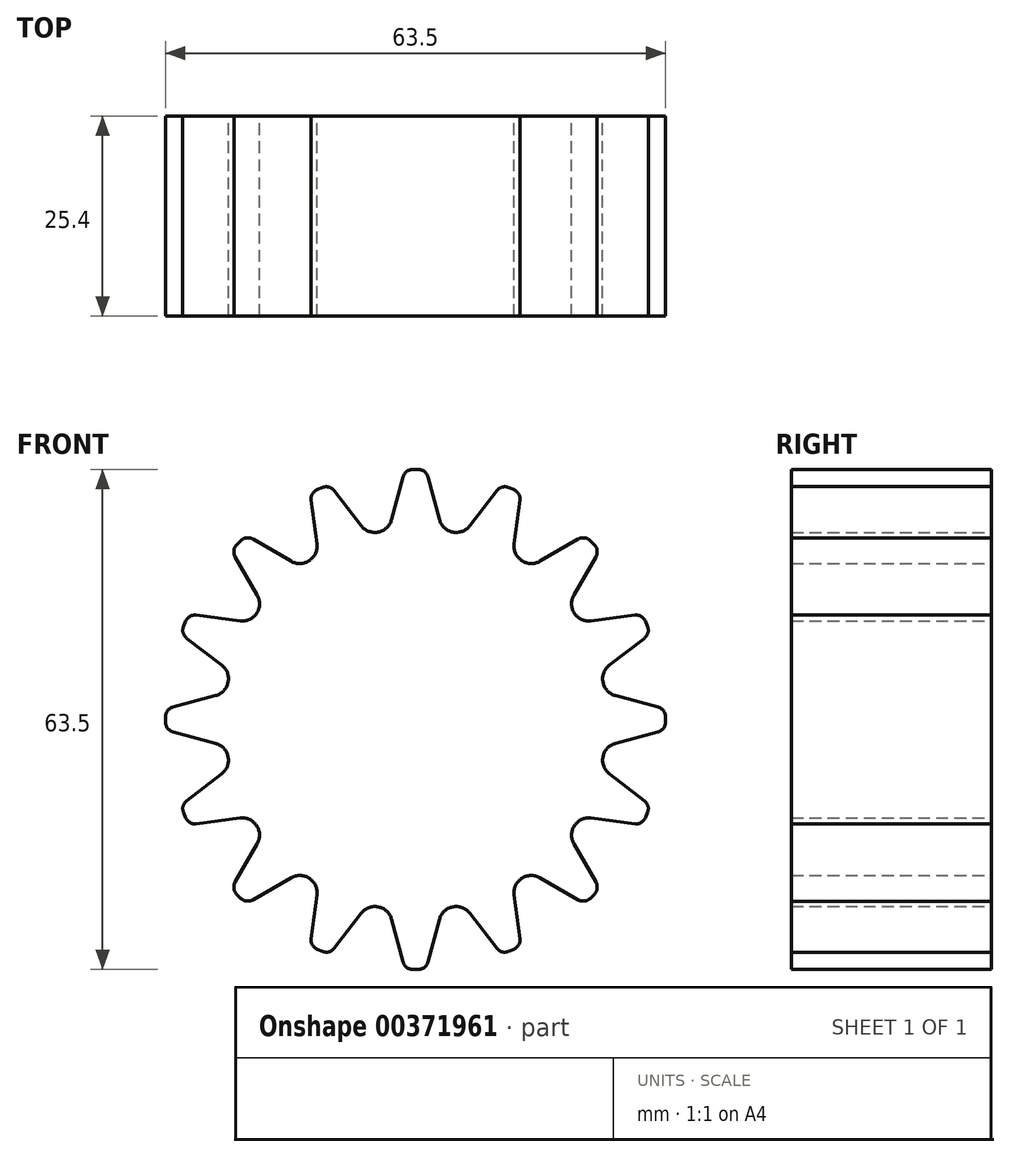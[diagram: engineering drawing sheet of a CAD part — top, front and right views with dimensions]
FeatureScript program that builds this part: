
annotation { "Feature Type Name" : "Feature", "Feature Type Description" : "" }
export const myFeature = defineFeature(function(context is Context, id is Id, definition is map)
    precondition{}
    {
        {
            var Q0;
            Q0=qCreatedBy(makeId("Front.planeOp"),FACE);
            var sketch = newSketch(context, id + "F0", { "sketchPlane" : qUnion([Q0])});
            skLineSegment(sketch, "E0", {"start": v(0, 39.03) * mm, "end": v(0, -39.4) * mm, "construction": true});
            skCircle(sketch, "E1", {"center": v(0, 0) * mm, "radius": 25.4 * mm, "construction": true});
            skLineSegment(sketch, "E2", {"start": v(0, 31.75) * mm, "end": v(-0.36, 31.75) * mm});
            skLineSegment(sketch, "E3", {"start": v(-1.59, 30.8) * mm, "end": v(-3.04, 25.4) * mm});
            skLineSegment(sketch, "E4.MirrorCS", {"start": v(0, 31.75) * mm, "end": v(0.36, 31.75) * mm});
            skLineSegment(sketch, "E5.MirrorCS", {"start": v(1.59, 30.8) * mm, "end": v(3.04, 25.4) * mm});
            skPoint(sketch, "E6.visualSharp", {"position": v(-1.34, 31.75) * mm});
            skArc(sketch, "E6.filletArc", {"start": v(-0.36, 31.75) * mm, "mid": v(-1.13, 31.49) * mm, "end": v(-1.59, 30.8) * mm});
            skPoint(sketch, "E7.visualSharp", {"position": v(1.34, 31.75) * mm});
            skArc(sketch, "E7.filletArc", {"start": v(1.59, 30.8) * mm, "mid": v(1.13, 31.49) * mm, "end": v(0.36, 31.75) * mm});
            skArc(sketch, "E8", {"start": v(3.04, 25.4) * mm, "mid": v(4.74, 23.8) * mm, "end": v(6.91, 24.63) * mm});
            skArc(sketch, "E9.MirrorCS", {"start": v(0.36, 31.75) * mm, "mid": v(1.13, 31.49) * mm, "end": v(1.59, 30.8) * mm});
            skArc(sketch, "E10.MirrorCS", {"start": v(-1.59, 30.8) * mm, "mid": v(-1.13, 31.49) * mm, "end": v(-0.36, 31.75) * mm});
            skLineSegment(sketch, "E11.1.0", {"start": v(-13.26, 27.86) * mm, "end": v(-12.53, 22.3) * mm});
            skArc(sketch, "E11.1.1", {"start": v(-6.91, 24.63) * mm, "mid": v(-4.74, 23.8) * mm, "end": v(-3.04, 25.4) * mm});
            skPoint(sketch, "E11.1.2", {"position": v(-10.92, 29.84) * mm});
            skLineSegment(sketch, "E11.1.3", {"start": v(-10.32, 29.07) * mm, "end": v(-6.91, 24.63) * mm});
            skPoint(sketch, "E11.1.4", {"position": v(-13.38, 28.82) * mm});
            skPoint(sketch, "E11.1.5", {"position": v(-13.38, 28.82) * mm});
            skPoint(sketch, "E11.1.6", {"position": v(-10.92, 29.84) * mm});
            skLineSegment(sketch, "E11.1.7", {"start": v(-13.26, 27.86) * mm, "end": v(-12.53, 22.3) * mm});
            skLineSegment(sketch, "E11.1.8", {"start": v(-10.32, 29.07) * mm, "end": v(-6.91, 24.63) * mm});
            skArc(sketch, "E11.1.9", {"start": v(-13.26, 27.86) * mm, "mid": v(-13.1, 28.66) * mm, "end": v(-12.48, 29.2) * mm});
            skArc(sketch, "E11.1.10", {"start": v(-11.82, 29.47) * mm, "mid": v(-11, 29.52) * mm, "end": v(-10.32, 29.07) * mm});
            skArc(sketch, "E11.1.11", {"start": v(-10.32, 29.07) * mm, "mid": v(-11, 29.52) * mm, "end": v(-11.82, 29.47) * mm});
            skArc(sketch, "E11.1.12", {"start": v(-12.48, 29.2) * mm, "mid": v(-13.1, 28.66) * mm, "end": v(-13.26, 27.86) * mm});
            skLineSegment(sketch, "E11.1.13", {"start": v(-12.15, 29.33) * mm, "end": v(-11.82, 29.47) * mm});
            skLineSegment(sketch, "E11.1.14", {"start": v(-12.15, 29.33) * mm, "end": v(-12.48, 29.2) * mm});
            skLineSegment(sketch, "E11.1.15", {"start": v(-12.15, 29.33) * mm, "end": v(-12.48, 29.2) * mm});
            skLineSegment(sketch, "E11.1.16", {"start": v(-12.15, 29.33) * mm, "end": v(-11.82, 29.47) * mm});
            skLineSegment(sketch, "E11.2.0", {"start": v(-22.9, 20.66) * mm, "end": v(-20.1, 15.81) * mm});
            skArc(sketch, "E11.2.1", {"start": v(-15.81, 20.1) * mm, "mid": v(-13.49, 20.18) * mm, "end": v(-12.53, 22.3) * mm});
            skPoint(sketch, "E11.2.2", {"position": v(-21.5, 23.4) * mm});
            skLineSegment(sketch, "E11.2.3", {"start": v(-20.66, 22.9) * mm, "end": v(-15.81, 20.1) * mm});
            skPoint(sketch, "E11.2.4", {"position": v(-23.4, 21.5) * mm});
            skPoint(sketch, "E11.2.5", {"position": v(-23.4, 21.5) * mm});
            skPoint(sketch, "E11.2.6", {"position": v(-21.5, 23.4) * mm});
            skLineSegment(sketch, "E11.2.7", {"start": v(-22.9, 20.66) * mm, "end": v(-20.1, 15.81) * mm});
            skLineSegment(sketch, "E11.2.8", {"start": v(-20.66, 22.9) * mm, "end": v(-15.81, 20.1) * mm});
            skArc(sketch, "E11.2.9", {"start": v(-22.9, 20.66) * mm, "mid": v(-23.07, 21.46) * mm, "end": v(-22.7, 22.2) * mm});
            skArc(sketch, "E11.2.10", {"start": v(-22.2, 22.7) * mm, "mid": v(-21.46, 23.07) * mm, "end": v(-20.66, 22.9) * mm});
            skArc(sketch, "E11.2.11", {"start": v(-20.66, 22.9) * mm, "mid": v(-21.46, 23.07) * mm, "end": v(-22.2, 22.7) * mm});
            skArc(sketch, "E11.2.12", {"start": v(-22.7, 22.2) * mm, "mid": v(-23.07, 21.46) * mm, "end": v(-22.9, 20.66) * mm});
            skLineSegment(sketch, "E11.2.13", {"start": v(-22.45, 22.45) * mm, "end": v(-22.2, 22.7) * mm});
            skLineSegment(sketch, "E11.2.14", {"start": v(-22.45, 22.45) * mm, "end": v(-22.7, 22.2) * mm});
            skLineSegment(sketch, "E11.2.15", {"start": v(-22.45, 22.45) * mm, "end": v(-22.7, 22.2) * mm});
            skLineSegment(sketch, "E11.2.16", {"start": v(-22.45, 22.45) * mm, "end": v(-22.2, 22.7) * mm});
            skLineSegment(sketch, "E11.3.0", {"start": v(-29.07, 10.32) * mm, "end": v(-24.63, 6.91) * mm});
            skArc(sketch, "E11.3.1", {"start": v(-22.3, 12.53) * mm, "mid": v(-20.18, 13.49) * mm, "end": v(-20.1, 15.81) * mm});
            skPoint(sketch, "E11.3.2", {"position": v(-28.82, 13.38) * mm});
            skLineSegment(sketch, "E11.3.3", {"start": v(-27.86, 13.26) * mm, "end": v(-22.3, 12.53) * mm});
            skPoint(sketch, "E11.3.4", {"position": v(-29.84, 10.92) * mm});
            skPoint(sketch, "E11.3.5", {"position": v(-29.84, 10.92) * mm});
            skPoint(sketch, "E11.3.6", {"position": v(-28.82, 13.38) * mm});
            skLineSegment(sketch, "E11.3.7", {"start": v(-29.07, 10.32) * mm, "end": v(-24.63, 6.91) * mm});
            skLineSegment(sketch, "E11.3.8", {"start": v(-27.86, 13.26) * mm, "end": v(-22.3, 12.53) * mm});
            skArc(sketch, "E11.3.9", {"start": v(-29.07, 10.32) * mm, "mid": v(-29.52, 11) * mm, "end": v(-29.47, 11.82) * mm});
            skArc(sketch, "E11.3.10", {"start": v(-29.2, 12.48) * mm, "mid": v(-28.66, 13.1) * mm, "end": v(-27.86, 13.26) * mm});
            skArc(sketch, "E11.3.11", {"start": v(-27.86, 13.26) * mm, "mid": v(-28.66, 13.1) * mm, "end": v(-29.2, 12.48) * mm});
            skArc(sketch, "E11.3.12", {"start": v(-29.47, 11.82) * mm, "mid": v(-29.52, 11) * mm, "end": v(-29.07, 10.32) * mm});
            skLineSegment(sketch, "E11.3.13", {"start": v(-29.33, 12.15) * mm, "end": v(-29.2, 12.48) * mm});
            skLineSegment(sketch, "E11.3.14", {"start": v(-29.33, 12.15) * mm, "end": v(-29.47, 11.82) * mm});
            skLineSegment(sketch, "E11.3.15", {"start": v(-29.33, 12.15) * mm, "end": v(-29.47, 11.82) * mm});
            skLineSegment(sketch, "E11.3.16", {"start": v(-29.33, 12.15) * mm, "end": v(-29.2, 12.48) * mm});
            skLineSegment(sketch, "E11.4.0", {"start": v(-30.8, -1.59) * mm, "end": v(-25.4, -3.04) * mm});
            skArc(sketch, "E11.4.1", {"start": v(-25.4, 3.04) * mm, "mid": v(-23.8, 4.74) * mm, "end": v(-24.63, 6.91) * mm});
            skPoint(sketch, "E11.4.2", {"position": v(-31.75, 1.34) * mm});
            skLineSegment(sketch, "E11.4.3", {"start": v(-30.8, 1.59) * mm, "end": v(-25.4, 3.04) * mm});
            skPoint(sketch, "E11.4.4", {"position": v(-31.75, -1.34) * mm});
            skPoint(sketch, "E11.4.5", {"position": v(-31.75, -1.34) * mm});
            skPoint(sketch, "E11.4.6", {"position": v(-31.75, 1.34) * mm});
            skLineSegment(sketch, "E11.4.7", {"start": v(-30.8, -1.59) * mm, "end": v(-25.4, -3.04) * mm});
            skLineSegment(sketch, "E11.4.8", {"start": v(-30.8, 1.59) * mm, "end": v(-25.4, 3.04) * mm});
            skArc(sketch, "E11.4.9", {"start": v(-30.8, -1.59) * mm, "mid": v(-31.49, -1.13) * mm, "end": v(-31.75, -0.36) * mm});
            skArc(sketch, "E11.4.10", {"start": v(-31.75, 0.36) * mm, "mid": v(-31.49, 1.13) * mm, "end": v(-30.8, 1.59) * mm});
            skArc(sketch, "E11.4.11", {"start": v(-30.8, 1.59) * mm, "mid": v(-31.49, 1.13) * mm, "end": v(-31.75, 0.36) * mm});
            skArc(sketch, "E11.4.12", {"start": v(-31.75, -0.36) * mm, "mid": v(-31.49, -1.13) * mm, "end": v(-30.8, -1.59) * mm});
            skLineSegment(sketch, "E11.4.13", {"start": v(-31.75, 0) * mm, "end": v(-31.75, 0.36) * mm});
            skLineSegment(sketch, "E11.4.14", {"start": v(-31.75, 0) * mm, "end": v(-31.75, -0.36) * mm});
            skLineSegment(sketch, "E11.4.15", {"start": v(-31.75, 0) * mm, "end": v(-31.75, -0.36) * mm});
            skLineSegment(sketch, "E11.4.16", {"start": v(-31.75, 0) * mm, "end": v(-31.75, 0.36) * mm});
            skLineSegment(sketch, "E11.5.0", {"start": v(-27.86, -13.26) * mm, "end": v(-22.3, -12.53) * mm});
            skArc(sketch, "E11.5.1", {"start": v(-24.63, -6.91) * mm, "mid": v(-23.8, -4.74) * mm, "end": v(-25.4, -3.04) * mm});
            skPoint(sketch, "E11.5.2", {"position": v(-29.84, -10.92) * mm});
            skLineSegment(sketch, "E11.5.3", {"start": v(-29.07, -10.32) * mm, "end": v(-24.63, -6.91) * mm});
            skPoint(sketch, "E11.5.4", {"position": v(-28.82, -13.38) * mm});
            skPoint(sketch, "E11.5.5", {"position": v(-28.82, -13.38) * mm});
            skPoint(sketch, "E11.5.6", {"position": v(-29.84, -10.92) * mm});
            skLineSegment(sketch, "E11.5.7", {"start": v(-27.86, -13.26) * mm, "end": v(-22.3, -12.53) * mm});
            skLineSegment(sketch, "E11.5.8", {"start": v(-29.07, -10.32) * mm, "end": v(-24.63, -6.91) * mm});
            skArc(sketch, "E11.5.9", {"start": v(-27.86, -13.26) * mm, "mid": v(-28.66, -13.1) * mm, "end": v(-29.2, -12.48) * mm});
            skArc(sketch, "E11.5.10", {"start": v(-29.47, -11.82) * mm, "mid": v(-29.52, -11) * mm, "end": v(-29.07, -10.32) * mm});
            skArc(sketch, "E11.5.11", {"start": v(-29.07, -10.32) * mm, "mid": v(-29.52, -11) * mm, "end": v(-29.47, -11.82) * mm});
            skArc(sketch, "E11.5.12", {"start": v(-29.2, -12.48) * mm, "mid": v(-28.66, -13.1) * mm, "end": v(-27.86, -13.26) * mm});
            skLineSegment(sketch, "E11.5.13", {"start": v(-29.33, -12.15) * mm, "end": v(-29.47, -11.82) * mm});
            skLineSegment(sketch, "E11.5.14", {"start": v(-29.33, -12.15) * mm, "end": v(-29.2, -12.48) * mm});
            skLineSegment(sketch, "E11.5.15", {"start": v(-29.33, -12.15) * mm, "end": v(-29.2, -12.48) * mm});
            skLineSegment(sketch, "E11.5.16", {"start": v(-29.33, -12.15) * mm, "end": v(-29.47, -11.82) * mm});
            skLineSegment(sketch, "E11.6.0", {"start": v(-20.66, -22.9) * mm, "end": v(-15.81, -20.1) * mm});
            skArc(sketch, "E11.6.1", {"start": v(-20.1, -15.81) * mm, "mid": v(-20.18, -13.49) * mm, "end": v(-22.3, -12.53) * mm});
            skPoint(sketch, "E11.6.2", {"position": v(-23.4, -21.5) * mm});
            skLineSegment(sketch, "E11.6.3", {"start": v(-22.9, -20.66) * mm, "end": v(-20.1, -15.81) * mm});
            skPoint(sketch, "E11.6.4", {"position": v(-21.5, -23.4) * mm});
            skPoint(sketch, "E11.6.5", {"position": v(-21.5, -23.4) * mm});
            skPoint(sketch, "E11.6.6", {"position": v(-23.4, -21.5) * mm});
            skLineSegment(sketch, "E11.6.7", {"start": v(-20.66, -22.9) * mm, "end": v(-15.81, -20.1) * mm});
            skLineSegment(sketch, "E11.6.8", {"start": v(-22.9, -20.66) * mm, "end": v(-20.1, -15.81) * mm});
            skArc(sketch, "E11.6.9", {"start": v(-20.66, -22.9) * mm, "mid": v(-21.46, -23.07) * mm, "end": v(-22.2, -22.7) * mm});
            skArc(sketch, "E11.6.10", {"start": v(-22.7, -22.2) * mm, "mid": v(-23.07, -21.46) * mm, "end": v(-22.9, -20.66) * mm});
            skArc(sketch, "E11.6.11", {"start": v(-22.9, -20.66) * mm, "mid": v(-23.07, -21.46) * mm, "end": v(-22.7, -22.2) * mm});
            skArc(sketch, "E11.6.12", {"start": v(-22.2, -22.7) * mm, "mid": v(-21.46, -23.07) * mm, "end": v(-20.66, -22.9) * mm});
            skLineSegment(sketch, "E11.6.13", {"start": v(-22.45, -22.45) * mm, "end": v(-22.7, -22.2) * mm});
            skLineSegment(sketch, "E11.6.14", {"start": v(-22.45, -22.45) * mm, "end": v(-22.2, -22.7) * mm});
            skLineSegment(sketch, "E11.6.15", {"start": v(-22.45, -22.45) * mm, "end": v(-22.2, -22.7) * mm});
            skLineSegment(sketch, "E11.6.16", {"start": v(-22.45, -22.45) * mm, "end": v(-22.7, -22.2) * mm});
            skLineSegment(sketch, "E11.7.0", {"start": v(-10.32, -29.07) * mm, "end": v(-6.91, -24.63) * mm});
            skArc(sketch, "E11.7.1", {"start": v(-12.53, -22.3) * mm, "mid": v(-13.49, -20.18) * mm, "end": v(-15.81, -20.1) * mm});
            skPoint(sketch, "E11.7.2", {"position": v(-13.38, -28.82) * mm});
            skLineSegment(sketch, "E11.7.3", {"start": v(-13.26, -27.86) * mm, "end": v(-12.53, -22.3) * mm});
            skPoint(sketch, "E11.7.4", {"position": v(-10.92, -29.84) * mm});
            skPoint(sketch, "E11.7.5", {"position": v(-10.92, -29.84) * mm});
            skPoint(sketch, "E11.7.6", {"position": v(-13.38, -28.82) * mm});
            skLineSegment(sketch, "E11.7.7", {"start": v(-10.32, -29.07) * mm, "end": v(-6.91, -24.63) * mm});
            skLineSegment(sketch, "E11.7.8", {"start": v(-13.26, -27.86) * mm, "end": v(-12.53, -22.3) * mm});
            skArc(sketch, "E11.7.9", {"start": v(-10.32, -29.07) * mm, "mid": v(-11, -29.52) * mm, "end": v(-11.82, -29.47) * mm});
            skArc(sketch, "E11.7.10", {"start": v(-12.48, -29.2) * mm, "mid": v(-13.1, -28.66) * mm, "end": v(-13.26, -27.86) * mm});
            skArc(sketch, "E11.7.11", {"start": v(-13.26, -27.86) * mm, "mid": v(-13.1, -28.66) * mm, "end": v(-12.48, -29.2) * mm});
            skArc(sketch, "E11.7.12", {"start": v(-11.82, -29.47) * mm, "mid": v(-11, -29.52) * mm, "end": v(-10.32, -29.07) * mm});
            skLineSegment(sketch, "E11.7.13", {"start": v(-12.15, -29.33) * mm, "end": v(-12.48, -29.2) * mm});
            skLineSegment(sketch, "E11.7.14", {"start": v(-12.15, -29.33) * mm, "end": v(-11.82, -29.47) * mm});
            skLineSegment(sketch, "E11.7.15", {"start": v(-12.15, -29.33) * mm, "end": v(-11.82, -29.47) * mm});
            skLineSegment(sketch, "E11.7.16", {"start": v(-12.15, -29.33) * mm, "end": v(-12.48, -29.2) * mm});
            skLineSegment(sketch, "E11.8.0", {"start": v(1.59, -30.8) * mm, "end": v(3.04, -25.4) * mm});
            skArc(sketch, "E11.8.1", {"start": v(-3.04, -25.4) * mm, "mid": v(-4.74, -23.8) * mm, "end": v(-6.91, -24.63) * mm});
            skPoint(sketch, "E11.8.2", {"position": v(-1.34, -31.75) * mm});
            skLineSegment(sketch, "E11.8.3", {"start": v(-1.59, -30.8) * mm, "end": v(-3.04, -25.4) * mm});
            skPoint(sketch, "E11.8.4", {"position": v(1.34, -31.75) * mm});
            skPoint(sketch, "E11.8.5", {"position": v(1.34, -31.75) * mm});
            skPoint(sketch, "E11.8.6", {"position": v(-1.34, -31.75) * mm});
            skLineSegment(sketch, "E11.8.7", {"start": v(1.59, -30.8) * mm, "end": v(3.04, -25.4) * mm});
            skLineSegment(sketch, "E11.8.8", {"start": v(-1.59, -30.8) * mm, "end": v(-3.04, -25.4) * mm});
            skArc(sketch, "E11.8.9", {"start": v(1.59, -30.8) * mm, "mid": v(1.13, -31.49) * mm, "end": v(0.36, -31.75) * mm});
            skArc(sketch, "E11.8.10", {"start": v(-0.36, -31.75) * mm, "mid": v(-1.13, -31.49) * mm, "end": v(-1.59, -30.8) * mm});
            skArc(sketch, "E11.8.11", {"start": v(-1.59, -30.8) * mm, "mid": v(-1.13, -31.49) * mm, "end": v(-0.36, -31.75) * mm});
            skArc(sketch, "E11.8.12", {"start": v(0.36, -31.75) * mm, "mid": v(1.13, -31.49) * mm, "end": v(1.59, -30.8) * mm});
            skLineSegment(sketch, "E11.8.13", {"start": v(0, -31.75) * mm, "end": v(-0.36, -31.75) * mm});
            skLineSegment(sketch, "E11.8.14", {"start": v(0, -31.75) * mm, "end": v(0.36, -31.75) * mm});
            skLineSegment(sketch, "E11.8.15", {"start": v(0, -31.75) * mm, "end": v(0.36, -31.75) * mm});
            skLineSegment(sketch, "E11.8.16", {"start": v(0, -31.75) * mm, "end": v(-0.36, -31.75) * mm});
            skLineSegment(sketch, "E11.9.0", {"start": v(13.26, -27.86) * mm, "end": v(12.53, -22.3) * mm});
            skArc(sketch, "E11.9.1", {"start": v(6.91, -24.63) * mm, "mid": v(4.74, -23.8) * mm, "end": v(3.04, -25.4) * mm});
            skPoint(sketch, "E11.9.2", {"position": v(10.92, -29.84) * mm});
            skLineSegment(sketch, "E11.9.3", {"start": v(10.32, -29.07) * mm, "end": v(6.91, -24.63) * mm});
            skPoint(sketch, "E11.9.4", {"position": v(13.38, -28.82) * mm});
            skPoint(sketch, "E11.9.5", {"position": v(13.38, -28.82) * mm});
            skPoint(sketch, "E11.9.6", {"position": v(10.92, -29.84) * mm});
            skLineSegment(sketch, "E11.9.7", {"start": v(13.26, -27.86) * mm, "end": v(12.53, -22.3) * mm});
            skLineSegment(sketch, "E11.9.8", {"start": v(10.32, -29.07) * mm, "end": v(6.91, -24.63) * mm});
            skArc(sketch, "E11.9.9", {"start": v(13.26, -27.86) * mm, "mid": v(13.1, -28.66) * mm, "end": v(12.48, -29.2) * mm});
            skArc(sketch, "E11.9.10", {"start": v(11.82, -29.47) * mm, "mid": v(11, -29.52) * mm, "end": v(10.32, -29.07) * mm});
            skArc(sketch, "E11.9.11", {"start": v(10.32, -29.07) * mm, "mid": v(11, -29.52) * mm, "end": v(11.82, -29.47) * mm});
            skArc(sketch, "E11.9.12", {"start": v(12.48, -29.2) * mm, "mid": v(13.1, -28.66) * mm, "end": v(13.26, -27.86) * mm});
            skLineSegment(sketch, "E11.9.13", {"start": v(12.15, -29.33) * mm, "end": v(11.82, -29.47) * mm});
            skLineSegment(sketch, "E11.9.14", {"start": v(12.15, -29.33) * mm, "end": v(12.48, -29.2) * mm});
            skLineSegment(sketch, "E11.9.15", {"start": v(12.15, -29.33) * mm, "end": v(12.48, -29.2) * mm});
            skLineSegment(sketch, "E11.9.16", {"start": v(12.15, -29.33) * mm, "end": v(11.82, -29.47) * mm});
            skLineSegment(sketch, "E11.10.0", {"start": v(22.9, -20.66) * mm, "end": v(20.1, -15.81) * mm});
            skArc(sketch, "E11.10.1", {"start": v(15.81, -20.1) * mm, "mid": v(13.49, -20.18) * mm, "end": v(12.53, -22.3) * mm});
            skPoint(sketch, "E11.10.2", {"position": v(21.5, -23.4) * mm});
            skLineSegment(sketch, "E11.10.3", {"start": v(20.66, -22.9) * mm, "end": v(15.81, -20.1) * mm});
            skPoint(sketch, "E11.10.4", {"position": v(23.4, -21.5) * mm});
            skPoint(sketch, "E11.10.5", {"position": v(23.4, -21.5) * mm});
            skPoint(sketch, "E11.10.6", {"position": v(21.5, -23.4) * mm});
            skLineSegment(sketch, "E11.10.7", {"start": v(22.9, -20.66) * mm, "end": v(20.1, -15.81) * mm});
            skLineSegment(sketch, "E11.10.8", {"start": v(20.66, -22.9) * mm, "end": v(15.81, -20.1) * mm});
            skArc(sketch, "E11.10.9", {"start": v(22.9, -20.66) * mm, "mid": v(23.07, -21.46) * mm, "end": v(22.7, -22.2) * mm});
            skArc(sketch, "E11.10.10", {"start": v(22.2, -22.7) * mm, "mid": v(21.46, -23.07) * mm, "end": v(20.66, -22.9) * mm});
            skArc(sketch, "E11.10.11", {"start": v(20.66, -22.9) * mm, "mid": v(21.46, -23.07) * mm, "end": v(22.2, -22.7) * mm});
            skArc(sketch, "E11.10.12", {"start": v(22.7, -22.2) * mm, "mid": v(23.07, -21.46) * mm, "end": v(22.9, -20.66) * mm});
            skLineSegment(sketch, "E11.10.13", {"start": v(22.45, -22.45) * mm, "end": v(22.2, -22.7) * mm});
            skLineSegment(sketch, "E11.10.14", {"start": v(22.45, -22.45) * mm, "end": v(22.7, -22.2) * mm});
            skLineSegment(sketch, "E11.10.15", {"start": v(22.45, -22.45) * mm, "end": v(22.7, -22.2) * mm});
            skLineSegment(sketch, "E11.10.16", {"start": v(22.45, -22.45) * mm, "end": v(22.2, -22.7) * mm});
            skLineSegment(sketch, "E11.11.0", {"start": v(29.07, -10.32) * mm, "end": v(24.63, -6.91) * mm});
            skArc(sketch, "E11.11.1", {"start": v(22.3, -12.53) * mm, "mid": v(20.18, -13.49) * mm, "end": v(20.1, -15.81) * mm});
            skPoint(sketch, "E11.11.2", {"position": v(28.82, -13.38) * mm});
            skLineSegment(sketch, "E11.11.3", {"start": v(27.86, -13.26) * mm, "end": v(22.3, -12.53) * mm});
            skPoint(sketch, "E11.11.4", {"position": v(29.84, -10.92) * mm});
            skPoint(sketch, "E11.11.5", {"position": v(29.84, -10.92) * mm});
            skPoint(sketch, "E11.11.6", {"position": v(28.82, -13.38) * mm});
            skLineSegment(sketch, "E11.11.7", {"start": v(29.07, -10.32) * mm, "end": v(24.63, -6.91) * mm});
            skLineSegment(sketch, "E11.11.8", {"start": v(27.86, -13.26) * mm, "end": v(22.3, -12.53) * mm});
            skArc(sketch, "E11.11.9", {"start": v(29.07, -10.32) * mm, "mid": v(29.52, -11) * mm, "end": v(29.47, -11.82) * mm});
            skArc(sketch, "E11.11.10", {"start": v(29.2, -12.48) * mm, "mid": v(28.66, -13.1) * mm, "end": v(27.86, -13.26) * mm});
            skArc(sketch, "E11.11.11", {"start": v(27.86, -13.26) * mm, "mid": v(28.66, -13.1) * mm, "end": v(29.2, -12.48) * mm});
            skArc(sketch, "E11.11.12", {"start": v(29.47, -11.82) * mm, "mid": v(29.52, -11) * mm, "end": v(29.07, -10.32) * mm});
            skLineSegment(sketch, "E11.11.13", {"start": v(29.33, -12.15) * mm, "end": v(29.2, -12.48) * mm});
            skLineSegment(sketch, "E11.11.14", {"start": v(29.33, -12.15) * mm, "end": v(29.47, -11.82) * mm});
            skLineSegment(sketch, "E11.11.15", {"start": v(29.33, -12.15) * mm, "end": v(29.47, -11.82) * mm});
            skLineSegment(sketch, "E11.11.16", {"start": v(29.33, -12.15) * mm, "end": v(29.2, -12.48) * mm});
            skLineSegment(sketch, "E11.12.0", {"start": v(30.8, 1.59) * mm, "end": v(25.4, 3.04) * mm});
            skArc(sketch, "E11.12.1", {"start": v(25.4, -3.04) * mm, "mid": v(23.8, -4.74) * mm, "end": v(24.63, -6.91) * mm});
            skPoint(sketch, "E11.12.2", {"position": v(31.75, -1.34) * mm});
            skLineSegment(sketch, "E11.12.3", {"start": v(30.8, -1.59) * mm, "end": v(25.4, -3.04) * mm});
            skPoint(sketch, "E11.12.4", {"position": v(31.75, 1.34) * mm});
            skPoint(sketch, "E11.12.5", {"position": v(31.75, 1.34) * mm});
            skPoint(sketch, "E11.12.6", {"position": v(31.75, -1.34) * mm});
            skLineSegment(sketch, "E11.12.7", {"start": v(30.8, 1.59) * mm, "end": v(25.4, 3.04) * mm});
            skLineSegment(sketch, "E11.12.8", {"start": v(30.8, -1.59) * mm, "end": v(25.4, -3.04) * mm});
            skArc(sketch, "E11.12.9", {"start": v(30.8, 1.59) * mm, "mid": v(31.49, 1.13) * mm, "end": v(31.75, 0.36) * mm});
            skArc(sketch, "E11.12.10", {"start": v(31.75, -0.36) * mm, "mid": v(31.49, -1.13) * mm, "end": v(30.8, -1.59) * mm});
            skArc(sketch, "E11.12.11", {"start": v(30.8, -1.59) * mm, "mid": v(31.49, -1.13) * mm, "end": v(31.75, -0.36) * mm});
            skArc(sketch, "E11.12.12", {"start": v(31.75, 0.36) * mm, "mid": v(31.49, 1.13) * mm, "end": v(30.8, 1.59) * mm});
            skLineSegment(sketch, "E11.12.13", {"start": v(31.75, 0) * mm, "end": v(31.75, -0.36) * mm});
            skLineSegment(sketch, "E11.12.14", {"start": v(31.75, 0) * mm, "end": v(31.75, 0.36) * mm});
            skLineSegment(sketch, "E11.12.15", {"start": v(31.75, 0) * mm, "end": v(31.75, 0.36) * mm});
            skLineSegment(sketch, "E11.12.16", {"start": v(31.75, 0) * mm, "end": v(31.75, -0.36) * mm});
            skLineSegment(sketch, "E11.13.0", {"start": v(27.86, 13.26) * mm, "end": v(22.3, 12.53) * mm});
            skArc(sketch, "E11.13.1", {"start": v(24.63, 6.91) * mm, "mid": v(23.8, 4.74) * mm, "end": v(25.4, 3.04) * mm});
            skPoint(sketch, "E11.13.2", {"position": v(29.84, 10.92) * mm});
            skLineSegment(sketch, "E11.13.3", {"start": v(29.07, 10.32) * mm, "end": v(24.63, 6.91) * mm});
            skPoint(sketch, "E11.13.4", {"position": v(28.82, 13.38) * mm});
            skPoint(sketch, "E11.13.5", {"position": v(28.82, 13.38) * mm});
            skPoint(sketch, "E11.13.6", {"position": v(29.84, 10.92) * mm});
            skLineSegment(sketch, "E11.13.7", {"start": v(27.86, 13.26) * mm, "end": v(22.3, 12.53) * mm});
            skLineSegment(sketch, "E11.13.8", {"start": v(29.07, 10.32) * mm, "end": v(24.63, 6.91) * mm});
            skArc(sketch, "E11.13.9", {"start": v(27.86, 13.26) * mm, "mid": v(28.66, 13.1) * mm, "end": v(29.2, 12.48) * mm});
            skArc(sketch, "E11.13.10", {"start": v(29.47, 11.82) * mm, "mid": v(29.52, 11) * mm, "end": v(29.07, 10.32) * mm});
            skArc(sketch, "E11.13.11", {"start": v(29.07, 10.32) * mm, "mid": v(29.52, 11) * mm, "end": v(29.47, 11.82) * mm});
            skArc(sketch, "E11.13.12", {"start": v(29.2, 12.48) * mm, "mid": v(28.66, 13.1) * mm, "end": v(27.86, 13.26) * mm});
            skLineSegment(sketch, "E11.13.13", {"start": v(29.33, 12.15) * mm, "end": v(29.47, 11.82) * mm});
            skLineSegment(sketch, "E11.13.14", {"start": v(29.33, 12.15) * mm, "end": v(29.2, 12.48) * mm});
            skLineSegment(sketch, "E11.13.15", {"start": v(29.33, 12.15) * mm, "end": v(29.2, 12.48) * mm});
            skLineSegment(sketch, "E11.13.16", {"start": v(29.33, 12.15) * mm, "end": v(29.47, 11.82) * mm});
            skLineSegment(sketch, "E11.14.0", {"start": v(20.66, 22.9) * mm, "end": v(15.81, 20.1) * mm});
            skArc(sketch, "E11.14.1", {"start": v(20.1, 15.81) * mm, "mid": v(20.18, 13.49) * mm, "end": v(22.3, 12.53) * mm});
            skPoint(sketch, "E11.14.2", {"position": v(23.4, 21.5) * mm});
            skLineSegment(sketch, "E11.14.3", {"start": v(22.9, 20.66) * mm, "end": v(20.1, 15.81) * mm});
            skPoint(sketch, "E11.14.4", {"position": v(21.5, 23.4) * mm});
            skPoint(sketch, "E11.14.5", {"position": v(21.5, 23.4) * mm});
            skPoint(sketch, "E11.14.6", {"position": v(23.4, 21.5) * mm});
            skLineSegment(sketch, "E11.14.7", {"start": v(20.66, 22.9) * mm, "end": v(15.81, 20.1) * mm});
            skLineSegment(sketch, "E11.14.8", {"start": v(22.9, 20.66) * mm, "end": v(20.1, 15.81) * mm});
            skArc(sketch, "E11.14.9", {"start": v(20.66, 22.9) * mm, "mid": v(21.46, 23.07) * mm, "end": v(22.2, 22.7) * mm});
            skArc(sketch, "E11.14.10", {"start": v(22.7, 22.2) * mm, "mid": v(23.07, 21.46) * mm, "end": v(22.9, 20.66) * mm});
            skArc(sketch, "E11.14.11", {"start": v(22.9, 20.66) * mm, "mid": v(23.07, 21.46) * mm, "end": v(22.7, 22.2) * mm});
            skArc(sketch, "E11.14.12", {"start": v(22.2, 22.7) * mm, "mid": v(21.46, 23.07) * mm, "end": v(20.66, 22.9) * mm});
            skLineSegment(sketch, "E11.14.13", {"start": v(22.45, 22.45) * mm, "end": v(22.7, 22.2) * mm});
            skLineSegment(sketch, "E11.14.14", {"start": v(22.45, 22.45) * mm, "end": v(22.2, 22.7) * mm});
            skLineSegment(sketch, "E11.14.15", {"start": v(22.45, 22.45) * mm, "end": v(22.2, 22.7) * mm});
            skLineSegment(sketch, "E11.14.16", {"start": v(22.45, 22.45) * mm, "end": v(22.7, 22.2) * mm});
            skLineSegment(sketch, "E11.15.0", {"start": v(10.32, 29.07) * mm, "end": v(6.91, 24.63) * mm});
            skArc(sketch, "E11.15.1", {"start": v(12.53, 22.3) * mm, "mid": v(13.49, 20.18) * mm, "end": v(15.81, 20.1) * mm});
            skPoint(sketch, "E11.15.2", {"position": v(13.38, 28.82) * mm});
            skLineSegment(sketch, "E11.15.3", {"start": v(13.26, 27.86) * mm, "end": v(12.53, 22.3) * mm});
            skPoint(sketch, "E11.15.4", {"position": v(10.92, 29.84) * mm});
            skPoint(sketch, "E11.15.5", {"position": v(10.92, 29.84) * mm});
            skPoint(sketch, "E11.15.6", {"position": v(13.38, 28.82) * mm});
            skLineSegment(sketch, "E11.15.7", {"start": v(10.32, 29.07) * mm, "end": v(6.91, 24.63) * mm});
            skLineSegment(sketch, "E11.15.8", {"start": v(13.26, 27.86) * mm, "end": v(12.53, 22.3) * mm});
            skArc(sketch, "E11.15.9", {"start": v(10.32, 29.07) * mm, "mid": v(11, 29.52) * mm, "end": v(11.82, 29.47) * mm});
            skArc(sketch, "E11.15.10", {"start": v(12.48, 29.2) * mm, "mid": v(13.1, 28.66) * mm, "end": v(13.26, 27.86) * mm});
            skArc(sketch, "E11.15.11", {"start": v(13.26, 27.86) * mm, "mid": v(13.1, 28.66) * mm, "end": v(12.48, 29.2) * mm});
            skArc(sketch, "E11.15.12", {"start": v(11.82, 29.47) * mm, "mid": v(11, 29.52) * mm, "end": v(10.32, 29.07) * mm});
            skLineSegment(sketch, "E11.15.13", {"start": v(12.15, 29.33) * mm, "end": v(12.48, 29.2) * mm});
            skLineSegment(sketch, "E11.15.14", {"start": v(12.15, 29.33) * mm, "end": v(11.82, 29.47) * mm});
            skLineSegment(sketch, "E11.15.15", {"start": v(12.15, 29.33) * mm, "end": v(11.82, 29.47) * mm});
            skLineSegment(sketch, "E11.15.16", {"start": v(12.15, 29.33) * mm, "end": v(12.48, 29.2) * mm});
            skSolve(sketch);
        }
        {
            var Q0;
            Q0=makeQuery(id+"F0.imprint","IMPRINT",FACE,{"disambiguationData":[TD([[makeQuery(id+"F0.imprint","IMPRINT",EDGE,{"derivedFrom":sQuery(id+"F0.wireOp",EDGE,"E8")}),-1.0]])]});
            extrude(context, id + "F1", {"entities" : qUnion([Q0]), "depth" : 25.4 * mm});
        }
    });
